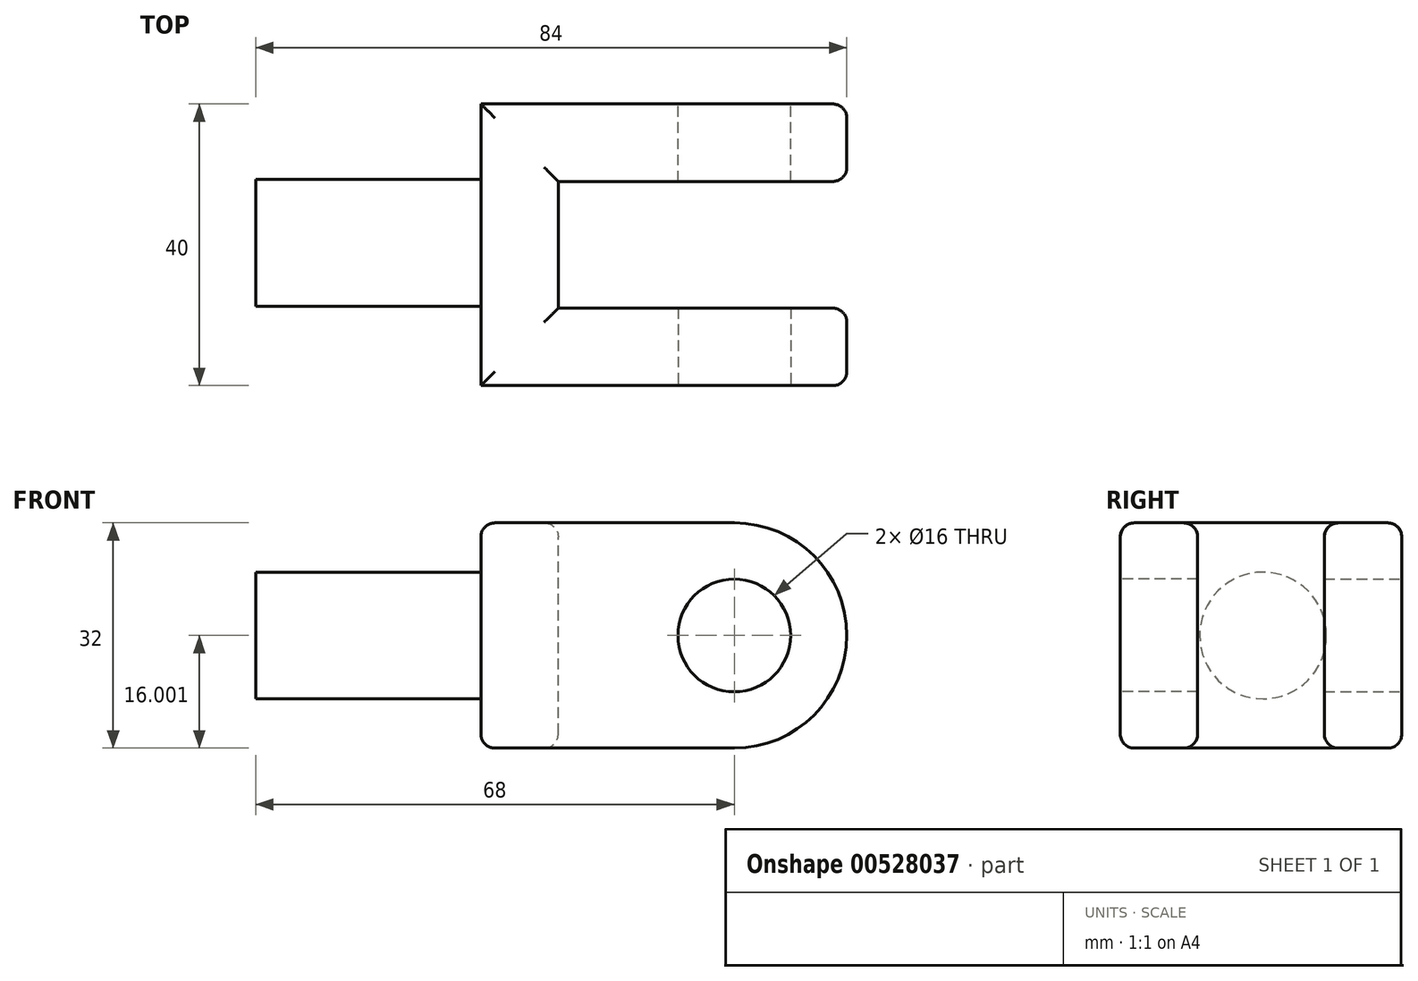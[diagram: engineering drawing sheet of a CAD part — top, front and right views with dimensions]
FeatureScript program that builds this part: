
annotation { "Feature Type Name" : "Feature", "Feature Type Description" : "" }
export const myFeature = defineFeature(function(context is Context, id is Id, definition is map)
    precondition{}
    {
        {
            var Q0;
            Q0=qCreatedBy(makeId("Right.planeOp"),FACE);
            var sketch = newSketch(context, id + "F0", { "sketchPlane" : qUnion([Q0])});
            skLineSegment(sketch, "E0", {"start": v(-20.29, 36.76) * mm, "end": v(19.71, 36.76) * mm});
            skLineSegment(sketch, "E1", {"start": v(19.71, 36.76) * mm, "end": v(19.71, 4.76) * mm});
            skLineSegment(sketch, "E2", {"start": v(19.71, 4.76) * mm, "end": v(-20.29, 4.76) * mm});
            skLineSegment(sketch, "E3", {"start": v(-20.29, 4.76) * mm, "end": v(-20.29, 36.76) * mm});
            skSolve(sketch);
        }
        {
            var Q0;
            Q0=makeQuery(id+"F0.imprint","IMPRINT",FACE,{"disambiguationData":[TD([[makeQuery(id+"F0.imprint","IMPRINT",EDGE,{"derivedFrom":sQuery(id+"F0.wireOp",EDGE,"E0")}),-1.0]])]});
            extrude(context, id + "F1", {"entities" : qUnion([Q0]), "depth" : 11 * mm, "offsetDistance" : 25.4 * mm});
        }
        {
            var Q0;
            Q0=makeQuery(id+"F1.opExtrude","SWEPT_FACE",FACE,{"disambiguationData":[OSD([sQuery(id+"F0.wireOp",EDGE,"E3")])]});
            var sketch = newSketch(context, id + "F2", { "sketchPlane" : qUnion([Q0])});
            skLineSegment(sketch, "E4", {"start": v(0, 4.76) * mm, "end": v(36, 4.76) * mm});
            skLineSegment(sketch, "E5", {"start": v(0, 36.76) * mm, "end": v(36, 36.76) * mm});
            skArc(sketch, "E6", {"start": v(36, 4.76) * mm, "mid": v(52, 20.76) * mm, "end": v(36, 36.76) * mm});
            skSolve(sketch);
        }
        {
            var Q0;
            Q0 = qSketchRegion(id + "F2", true);
            var Q1;
            {var subQ2=sQuery(id+"F2.wireOp",EDGE,"E6");Q1=makeQuery(id+"F2.imprint","IMPRINT",FACE,{"disambiguationData":[TD([[makeQuery(id+"F2.imprint","IMPRINT",EDGE,{"derivedFrom":subQ2}),1.0]])]});}
            extrude(context, id + "F3", {"entities" : qUnion([Q0, Q1]), "operationType" : NewBodyOperationType.ADD, "oppositeDirection" : true, "depth" : 11 * mm, "offsetDistance" : 25.4 * mm});
        }
        {
            var Q0;
            {var subQ0=sQuery(id+"F0.wireOp",EDGE,"E3");Q0=makeQuery(id+"F3.boolean.opBoolean","MERGE",FACE,{"derivedFrom":[makeQuery(id+"F1.opExtrude","SWEPT_FACE",FACE,{"disambiguationData":[OSD([subQ0])]}),makeQuery(id+"F3.opExtrude","CAP_FACE",FACE,{"disambiguationData":[OSD([subQ0,sQuery(id+"F2.wireOp",EDGE,"E4"),sQuery(id+"F2.wireOp",EDGE,"E5"),sQuery(id+"F2.wireOp",EDGE,"E6")])],"isStart":true})]});}
            var sketch = newSketch(context, id + "F4", { "sketchPlane" : qUnion([Q0])});
            skCircle(sketch, "E7", {"center": v(36, 20.76) * mm, "radius": 8 * mm});
            skSolve(sketch);
        }
        {
            var Q0;
            Q0=makeQuery(id+"F4.imprint","IMPRINT",FACE,{"disambiguationData":[TD([[makeQuery(id+"F4.imprint","IMPRINT",EDGE,{"derivedFrom":sQuery(id+"F4.wireOp",EDGE,"E7")}),1.0]])]});
            extrude(context, id + "F5", {"entities" : qUnion([Q0]), "operationType" : NewBodyOperationType.REMOVE, "oppositeDirection" : true, "depth" : 76.2 * mm, "offsetDistance" : 25.4 * mm});
        }
        {
            var Q0;
            Q0=makeQuery(id+"F1.opExtrude","SWEPT_FACE",FACE,{"disambiguationData":[OSD([sQuery(id+"F0.wireOp",EDGE,"E1")])]});
            var sketch = newSketch(context, id + "F6", { "sketchPlane" : qUnion([Q0])});
            skLineSegment(sketch, "E8", {"start": v(0, 36.76) * mm, "end": v(-36, 36.76) * mm});
            skPoint(sketch, "E8.endSnap0", {"position": v(-5.5, 36.76) * mm});
            skLineSegment(sketch, "E9", {"start": v(0, 4.76) * mm, "end": v(-36, 4.76) * mm});
            skArc(sketch, "E10", {"start": v(-36, 36.76) * mm, "mid": v(-52, 20.76) * mm, "end": v(-36, 4.76) * mm});
            skSolve(sketch);
        }
        {
            var Q0;
            Q0 = qSketchRegion(id + "F6", true);
            var Q1;
            {var subQ2=sQuery(id+"F6.wireOp",EDGE,"E10");Q1=makeQuery(id+"F6.imprint","IMPRINT",FACE,{"disambiguationData":[TD([[makeQuery(id+"F6.imprint","IMPRINT",EDGE,{"derivedFrom":subQ2}),1.0]])]});}
            extrude(context, id + "F7", {"entities" : qUnion([Q0, Q1]), "operationType" : NewBodyOperationType.ADD, "oppositeDirection" : true, "depth" : 11 * mm, "offsetDistance" : 25.4 * mm});
        }
        {
            var Q0;
            Q0=makeQuery(id+"F7.opExtrude","CAP_FACE",FACE,{"disambiguationData":[OSD([sQuery(id+"F0.wireOp",EDGE,"E1"),sQuery(id+"F6.wireOp",EDGE,"E8"),sQuery(id+"F6.wireOp",EDGE,"E9"),sQuery(id+"F6.wireOp",EDGE,"E10")])],"isStart":true});
            var sketch = newSketch(context, id + "F8", { "sketchPlane" : qUnion([Q0])});
            skCircle(sketch, "E11", {"center": v(-36, 20.76) * mm, "radius": 8 * mm});
            skSolve(sketch);
        }
        {
            var Q0;
            Q0=makeQuery(id+"F8.imprint","IMPRINT",FACE,{"disambiguationData":[TD([[makeQuery(id+"F8.imprint","IMPRINT",EDGE,{"derivedFrom":sQuery(id+"F8.wireOp",EDGE,"E11")}),1.0]])]});
            extrude(context, id + "F9", {"entities" : qUnion([Q0]), "operationType" : NewBodyOperationType.REMOVE, "oppositeDirection" : true, "depth" : 76.2 * mm, "offsetDistance" : 25.4 * mm});
        }
        {
            var Q0;
            Q0=makeQuery(id+"F7.opExtrude","SWEPT_FACE",FACE,{"disambiguationData":[OSD([sQuery(id+"F6.wireOp",EDGE,"E10")])]});
            var Q1;
            Q1=makeQuery(id+"F3.opExtrude","SWEPT_FACE",FACE,{"disambiguationData":[OSD([sQuery(id+"F2.wireOp",EDGE,"E6")])]});
            var Q2;
            Q2=makeQuery(id+"F3.boolean.opBoolean","MERGE",FACE,{"derivedFrom":[makeQuery(id+"F1.opExtrude","SWEPT_FACE",FACE,{"disambiguationData":[OSD([sQuery(id+"F0.wireOp",EDGE,"E0")])]}),makeQuery(id+"F3.opExtrude","SWEPT_FACE",FACE,{"disambiguationData":[OSD([sQuery(id+"F2.wireOp",EDGE,"E5")])]})]});
            var Q3;
            Q3=makeQuery(id+"F3.boolean.opBoolean","MERGE",FACE,{"derivedFrom":[makeQuery(id+"F1.opExtrude","SWEPT_FACE",FACE,{"disambiguationData":[OSD([sQuery(id+"F0.wireOp",EDGE,"E2")])]}),makeQuery(id+"F3.opExtrude","SWEPT_FACE",FACE,{"disambiguationData":[OSD([sQuery(id+"F2.wireOp",EDGE,"E4")])]})]});
            fillet(context, id + "F10", {"entities" : qUnion([Q0, Q1, Q2, Q3]), "radius" : 2 * mm, "tangentPropagation" : true, "allowEdgeOverflow" : false});
        }
        {
            var Q0;
            Q0=makeQuery(id+"F1.opExtrude","CAP_FACE",FACE,{"disambiguationData":[OSD([sQuery(id+"F0.wireOp",EDGE,"E0"),sQuery(id+"F0.wireOp",EDGE,"E1"),sQuery(id+"F0.wireOp",EDGE,"E2"),sQuery(id+"F0.wireOp",EDGE,"E3")])],"isStart":true});
            var sketch = newSketch(context, id + "F11", { "sketchPlane" : qUnion([Q0])});
            skCircle(sketch, "E12", {"center": v(0, 20.76) * mm, "radius": 9 * mm});
            skPoint(sketch, "E12.centerSnap0", {"position": v(-19.71, 20.76) * mm});
            skSolve(sketch);
        }
        {
            var Q0;
            Q0 = qSketchRegion(id + "F11", true);
            extrude(context, id + "F12", {"entities" : qUnion([Q0]), "operationType" : NewBodyOperationType.ADD, "depth" : 32 * mm, "offsetDistance" : 25.4 * mm});
        }
        {
            var Q0;
            {var subQ0=sQuery(id+"F0.wireOp",EDGE,"E1");Q0=makeQuery(id+"F7.boolean.opBoolean","MERGE",FACE,{"derivedFrom":[makeQuery(id+"F1.opExtrude","SWEPT_FACE",FACE,{"disambiguationData":[OSD([subQ0])]}),makeQuery(id+"F7.opExtrude","CAP_FACE",FACE,{"disambiguationData":[OSD([subQ0,sQuery(id+"F6.wireOp",EDGE,"E8"),sQuery(id+"F6.wireOp",EDGE,"E9"),sQuery(id+"F6.wireOp",EDGE,"E10")])],"isStart":true})]});}
            var sketch = newSketch(context, id + "F13", { "sketchPlane" : qUnion([Q0])});
            skCircle(sketch, "E13", {"center": v(-36, 20.76) * mm, "radius": 8 * mm});
            skSolve(sketch);
        }
        {
            var Q0;
            Q0=makeQuery(id+"F13.imprint","IMPRINT",FACE,{"disambiguationData":[TD([[makeQuery(id+"F13.imprint","IMPRINT",EDGE,{"derivedFrom":sQuery(id+"F13.wireOp",EDGE,"E13")}),1.0]])]});
            extrude(context, id + "F14", {"entities" : qUnion([Q0]), "operationType" : NewBodyOperationType.REMOVE, "oppositeDirection" : true, "depth" : 36.07 * mm, "offsetDistance" : 25.4 * mm});
        }
    });
